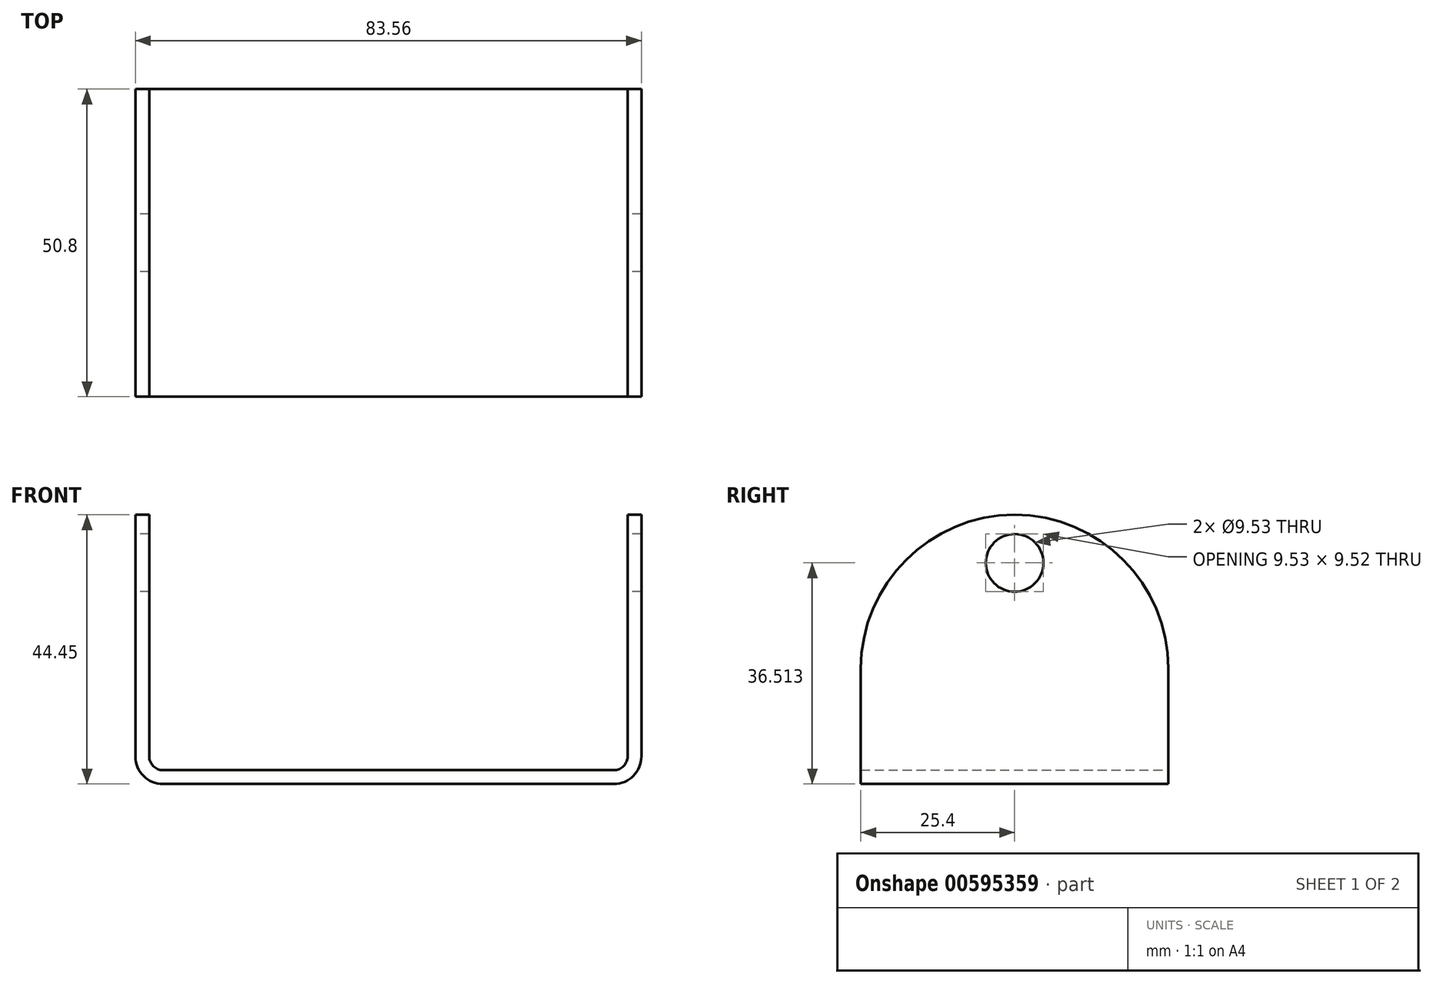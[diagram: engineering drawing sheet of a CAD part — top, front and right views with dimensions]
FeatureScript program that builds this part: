
annotation { "Feature Type Name" : "Feature", "Feature Type Description" : "" }
export const myFeature = defineFeature(function(context is Context, id is Id, definition is map)
    precondition{}
    {
        {
            var Q0;
            Q0=qCreatedBy(makeId("Front.planeOp"),FACE);
            var sketch = newSketch(context, id + "F0", { "sketchPlane" : qUnion([Q0])});
            skLineSegment(sketch, "E0", {"start": v(-37.21, 0) * mm, "end": v(37.21, 0) * mm});
            skLineSegment(sketch, "E1", {"start": v(-41.78, 4.57) * mm, "end": v(-41.78, 44.45) * mm});
            skLineSegment(sketch, "E2", {"start": v(-41.78, 44.45) * mm, "end": v(-39.5, 44.45) * mm});
            skLineSegment(sketch, "E3", {"start": v(-39.5, 44.45) * mm, "end": v(-39.5, 4.57) * mm});
            skLineSegment(sketch, "E4", {"start": v(-37.21, 2.29) * mm, "end": v(37.21, 2.29) * mm});
            skLineSegment(sketch, "E5", {"start": v(39.5, 4.57) * mm, "end": v(39.5, 44.45) * mm});
            skLineSegment(sketch, "E6", {"start": v(39.5, 44.45) * mm, "end": v(41.78, 44.45) * mm});
            skLineSegment(sketch, "E7", {"start": v(41.78, 44.45) * mm, "end": v(41.78, 4.57) * mm});
            skPoint(sketch, "E8.visualSharp", {"position": v(-39.5, 2.29) * mm});
            skArc(sketch, "E8.filletArc", {"start": v(-39.5, 4.57) * mm, "mid": v(-38.83, 2.96) * mm, "end": v(-37.21, 2.29) * mm});
            skPoint(sketch, "E9.visualSharp", {"position": v(39.5, 2.29) * mm});
            skArc(sketch, "E9.filletArc", {"start": v(37.21, 2.29) * mm, "mid": v(38.83, 2.96) * mm, "end": v(39.5, 4.57) * mm});
            skPoint(sketch, "E10.visualSharp", {"position": v(-41.78, 0) * mm});
            skArc(sketch, "E10.filletArc", {"start": v(-41.78, 4.57) * mm, "mid": v(-40.44, 1.34) * mm, "end": v(-37.21, 0) * mm});
            skPoint(sketch, "E11.visualSharp", {"position": v(41.78, 0) * mm});
            skArc(sketch, "E11.filletArc", {"start": v(37.21, 0) * mm, "mid": v(40.44, 1.34) * mm, "end": v(41.78, 4.57) * mm});
            skPoint(sketch, "E12", {"position": v(0, 0) * mm});
            skSolve(sketch);
        }
        {
            var Q0;
            Q0=makeQuery(id+"F0.imprint","IMPRINT",FACE,{"disambiguationData":[TD([[makeQuery(id+"F0.imprint","IMPRINT",EDGE,{"derivedFrom":sQuery(id+"F0.wireOp",EDGE,"E0")}),1.0]])]});
            extrude(context, id + "F1", {"entities" : qUnion([Q0]), "endBound" : BoundingType.SYMMETRIC, "depth" : 50.8 * mm, "offsetDistance" : 25.4 * mm});
        }
        {
            var Q0;
            Q0=makeQuery(id+"F1.opExtrude","SWEPT_FACE",FACE,{"disambiguationData":[OSD([sQuery(id+"F0.wireOp",EDGE,"E1")])]});
            var sketch = newSketch(context, id + "F2", { "sketchPlane" : qUnion([Q0])});
            skArc(sketch, "E13", {"start": v(25.4, 19.05) * mm, "mid": v(0, 44.45) * mm, "end": v(-25.4, 19.05) * mm});
            skLineSegment(sketch, "E14", {"start": v(25.4, 19.05) * mm, "end": v(25.4, 44.45) * mm});
            skLineSegment(sketch, "E15", {"start": v(25.4, 44.45) * mm, "end": v(-25.4, 44.45) * mm});
            skLineSegment(sketch, "E16", {"start": v(-25.4, 44.45) * mm, "end": v(-25.4, 19.05) * mm});
            skCircle(sketch, "E17", {"center": v(0, 36.51) * mm, "radius": 4.76 * mm});
            skSolve(sketch);
        }
        {
            var Q0;
            {var subQ0=sQuery(id+"F2.wireOp",EDGE,"E16");Q0=makeQuery(id+"F2.imprint","IMPRINT",FACE,{"disambiguationData":[TD([[makeQuery(id+"F2.imprint","IMPRINT",EDGE,{"derivedFrom":subQ0}),-1.0]])]});}
            var Q1;
            Q1=makeQuery(id+"F2.imprint","IMPRINT",FACE,{"disambiguationData":[TD([[makeQuery(id+"F2.imprint","IMPRINT",EDGE,{"derivedFrom":sQuery(id+"F2.wireOp",EDGE,"E17")}),1.0]])]});
            var Q2;
            {var subQ0=sQuery(id+"F2.wireOp",EDGE,"E14");Q2=makeQuery(id+"F2.imprint","IMPRINT",FACE,{"disambiguationData":[TD([[makeQuery(id+"F2.imprint","IMPRINT",EDGE,{"derivedFrom":subQ0}),1.0]])]});}
            extrude(context, id + "F3", {"entities" : qUnion([Q0, Q1, Q2]), "operationType" : NewBodyOperationType.REMOVE, "endBound" : BoundingType.THROUGH_ALL, "oppositeDirection" : true, "depth" : 25.4 * mm, "offsetDistance" : 25.4 * mm});
        }
    });
